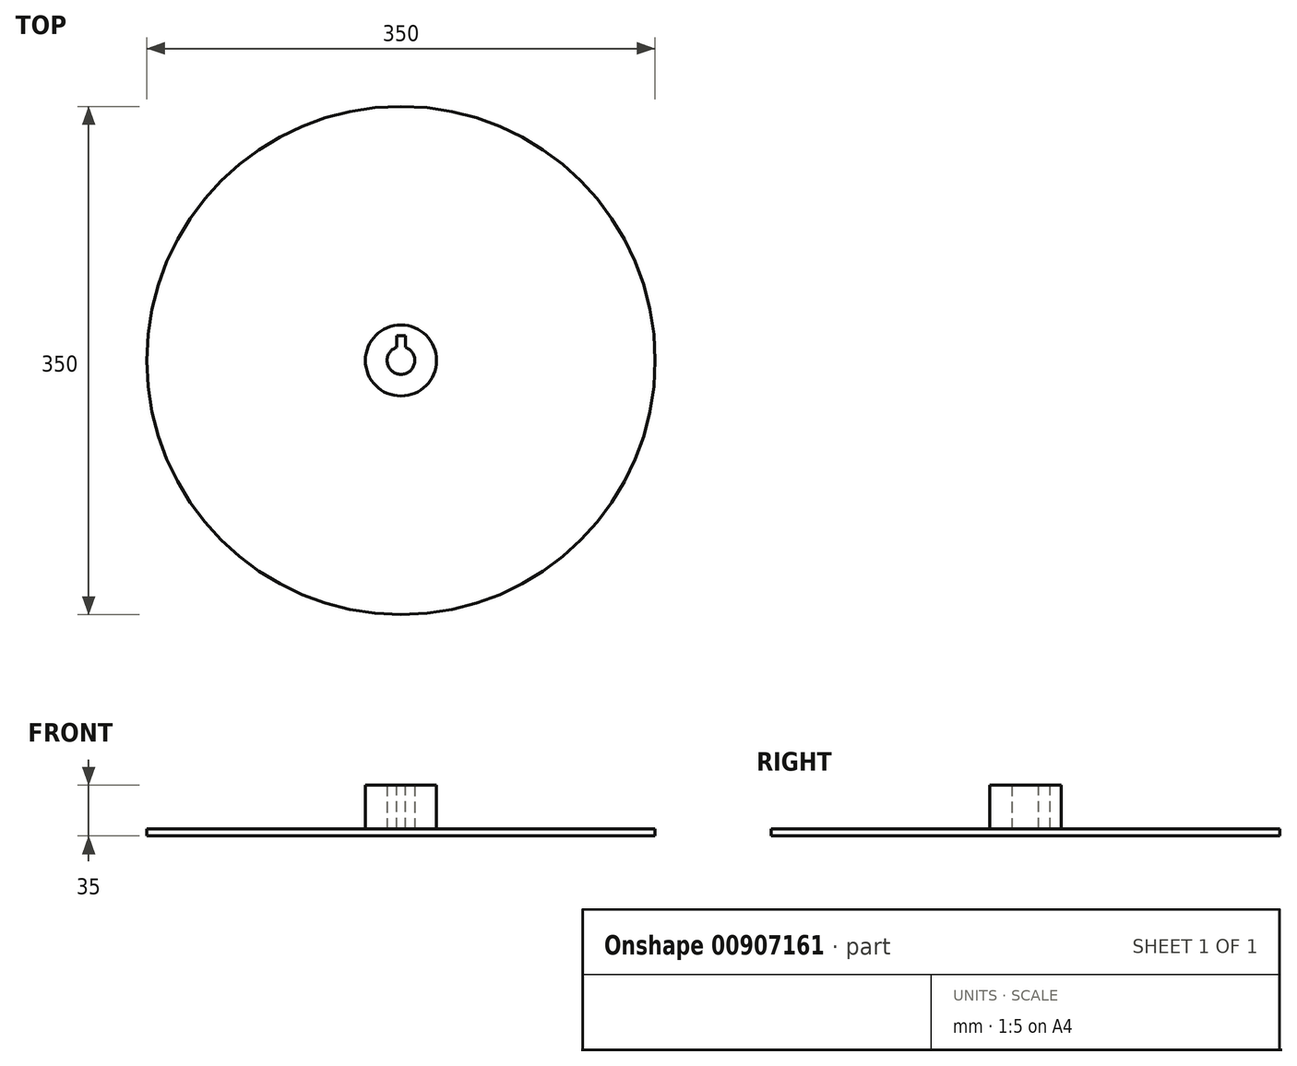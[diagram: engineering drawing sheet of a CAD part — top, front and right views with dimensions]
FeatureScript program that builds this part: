
annotation { "Feature Type Name" : "Feature", "Feature Type Description" : "" }
export const myFeature = defineFeature(function(context is Context, id is Id, definition is map)
    precondition{}
    {
        {
            var Q0;
            Q0=qCreatedBy(makeId("Front.planeOp"),FACE);
            var sketch = newSketch(context, id + "F0", { "sketchPlane" : qUnion([Q0])});
            skLineSegment(sketch, "E0", {"start": v(175, 0) * mm, "end": v(175, 5) * mm});
            skLineSegment(sketch, "E1", {"start": v(175, 5) * mm, "end": v(24.5, 5) * mm});
            skLineSegment(sketch, "E2", {"start": v(24.5, 5) * mm, "end": v(24.5, 35) * mm});
            skLineSegment(sketch, "E3", {"start": v(24.5, 35) * mm, "end": v(9.5, 35) * mm});
            skLineSegment(sketch, "E4", {"start": v(0, 0) * mm, "end": v(0, 69.26) * mm, "construction": true});
            skLineSegment(sketch, "E5", {"start": v(9.5, 35) * mm, "end": v(9.5, 5) * mm});
            skLineSegment(sketch, "E6", {"start": v(9.5, 5) * mm, "end": v(0, 5) * mm});
            skLineSegment(sketch, "E7", {"start": v(0, 5) * mm, "end": v(0, 0) * mm});
            skLineSegment(sketch, "E8", {"start": v(175, 0) * mm, "end": v(0, 0) * mm});
            skSolve(sketch);
        }
        {
            var Q0;
            Q0=makeQuery(id+"F0.imprint","IMPRINT",FACE,{"disambiguationData":[TD([[makeQuery(id+"F0.imprint","IMPRINT",EDGE,{"derivedFrom":sQuery(id+"F0.wireOp",EDGE,"E0")}),1.0]])]});
            var Q1;
            Q1=sQuery(id+"F0.wireOp",EDGE,"E4");
            revolve(context, id + "F1", {"surfaceOperationType" : NewSurfaceOperationType.NEW, "entities" : qUnion([Q0]), "axis" : qUnion([Q1]), "revolveType" : RevolveType.FULL});
        }
        {
            var Q0;
            Q0=makeQuery(id+"F1.opRevolve","SWEPT_FACE",FACE,{"disambiguationData":[OSD([sQuery(id+"F0.wireOp",EDGE,"E3")])]});
            var sketch = newSketch(context, id + "F2", { "sketchPlane" : qUnion([Q0])});
            skLineSegment(sketch, "E9.bottom", {"start": v(-3, 0) * mm, "end": v(3, 0) * mm});
            skLineSegment(sketch, "E9.top", {"start": v(-3, 17) * mm, "end": v(3, 17) * mm});
            skLineSegment(sketch, "E9.left", {"start": v(-3, 0) * mm, "end": v(-3, 17) * mm});
            skLineSegment(sketch, "E9.right", {"start": v(3, 0) * mm, "end": v(3, 17) * mm});
            skLineSegment(sketch, "E10", {"start": v(0, 9.5) * mm, "end": v(0, 24.5) * mm, "construction": true});
            skPoint(sketch, "E11", {"position": v(0, 17) * mm});
            skSolve(sketch);
        }
        {
            var Q0;
            {var subQ0=sQuery(id+"F2.wireOp",EDGE,"E9.top");Q0=makeQuery(id+"F2.imprint","IMPRINT",FACE,{"disambiguationData":[TD([[makeQuery(id+"F2.imprint","IMPRINT",EDGE,{"derivedFrom":subQ0}),-1.0]])]});}
            extrude(context, id + "F3", {"entities" : qUnion([Q0]), "operationType" : NewBodyOperationType.REMOVE, "oppositeDirection" : true, "depth" : 30 * mm, "offsetDistance" : 25 * mm});
        }
    });
